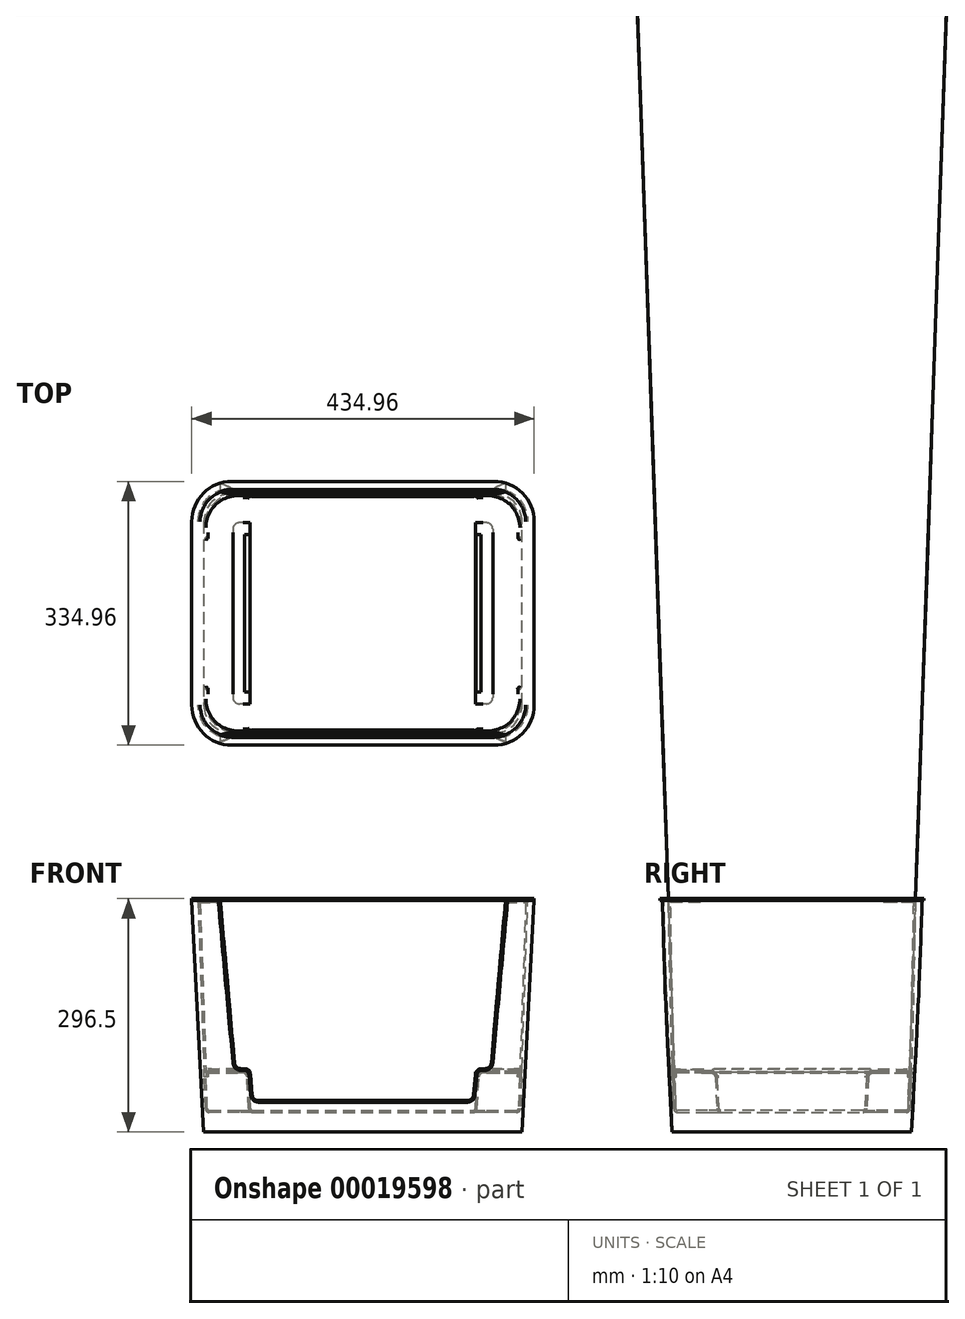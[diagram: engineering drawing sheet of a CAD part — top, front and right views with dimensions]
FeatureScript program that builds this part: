
annotation { "Feature Type Name" : "Feature", "Feature Type Description" : "" }
export const myFeature = defineFeature(function(context is Context, id is Id, definition is map)
    precondition{}
    {
        {
            var Q0;
            Q0=qCreatedBy(makeId("Front.planeOp"),FACE);
            var sketch = newSketch(context, id + "F0", { "sketchPlane" : qUnion([Q0])});
            skLineSegment(sketch, "E0.rect.bottom", {"start": v(150, -100) * mm, "end": v(-150, -100) * mm});
            skLineSegment(sketch, "E0.rect.top", {"start": v(150, 100) * mm, "end": v(-150, 100) * mm});
            skLineSegment(sketch, "E0.rect.left", {"start": v(150, -100) * mm, "end": v(150, 100) * mm});
            skLineSegment(sketch, "E0.rect.right", {"start": v(-150, -100) * mm, "end": v(-150, 100) * mm});
            skPoint(sketch, "E0.rect.middle", {"position": v(0, 0) * mm});
            skSolve(sketch);
        }
        {
            var Q0;
            Q0 = qSketchRegion(id + "F0", true);
            extrude(context, id + "F1", {"entities" : qUnion([Q0]), "endBound" : BoundingType.SYMMETRIC, "depth" : 200 * mm});
        }
        {
            var Q0;
            Q0=makeQuery(id+"F1.opExtrude","SWEPT_FACE",FACE,{"disambiguationData":[OSD([sQuery(id+"F0.wireOp",EDGE,"E0.rect.bottom")])]});
            var sketch = newSketch(context, id + "F2", { "sketchPlane" : qUnion([Q0])});
            skLineSegment(sketch, "E1.rect.bottom", {"start": v(165, -115) * mm, "end": v(-165, -115) * mm});
            skLineSegment(sketch, "E1.rect.top", {"start": v(165, 115) * mm, "end": v(-165, 115) * mm});
            skLineSegment(sketch, "E1.rect.left", {"start": v(165, -115) * mm, "end": v(165, 115) * mm});
            skLineSegment(sketch, "E1.rect.right", {"start": v(-165, -115) * mm, "end": v(-165, 115) * mm});
            skPoint(sketch, "E1.rect.middle", {"position": v(0, 0) * mm});
            skSolve(sketch);
        }
        {
            var Q0;
            Q0 = qSketchRegion(id + "F2", true);
            extrude(context, id + "F3", {"entities" : qUnion([Q0]), "depth" : 1.5 * mm});
        }
        {
            var Q0;
            Q0=makeQuery(id+"F3.opExtrude","SWEPT_EDGE",EDGE,{"disambiguationData":[OSD([sQuery(id+"F2.wireOp",EDGE,"E1.rect.top"),sQuery(id+"F2.wireOp",EDGE,"E1.rect.right")])]});
            var Q1;
            Q1=makeQuery(id+"F3.opExtrude","SWEPT_EDGE",EDGE,{"disambiguationData":[OSD([sQuery(id+"F2.wireOp",EDGE,"E1.rect.bottom"),sQuery(id+"F2.wireOp",EDGE,"E1.rect.right")])]});
            var Q2;
            Q2=makeQuery(id+"F3.opExtrude","SWEPT_EDGE",EDGE,{"disambiguationData":[OSD([sQuery(id+"F2.wireOp",EDGE,"E1.rect.top"),sQuery(id+"F2.wireOp",EDGE,"E1.rect.left")])]});
            var Q3;
            Q3=makeQuery(id+"F3.opExtrude","SWEPT_EDGE",EDGE,{"disambiguationData":[OSD([sQuery(id+"F2.wireOp",EDGE,"E1.rect.bottom"),sQuery(id+"F2.wireOp",EDGE,"E1.rect.left")])]});
            fillet(context, id + "F4", {"entities" : qUnion([Q0, Q1, Q2, Q3]), "radius" : 8 * mm, "tangentPropagation" : true, "allowEdgeOverflow" : false});
        }
        {
            var Q0;
            Q0=makeQuery(id+"F3.opExtrude","CAP_FACE",FACE,{"disambiguationData":[OSD([sQuery(id+"F2.wireOp",EDGE,"E1.rect.bottom"),sQuery(id+"F2.wireOp",EDGE,"E1.rect.top"),sQuery(id+"F2.wireOp",EDGE,"E1.rect.left"),sQuery(id+"F2.wireOp",EDGE,"E1.rect.right")])],"isStart":false});
            cPlane(context, id + "F5", {"entities" : qUnion([Q0]), "cplaneType" : CPlaneType.OFFSET, "offset" : 50 * mm, "width" : 150 * mm, "height" : 150 * mm});
        }
        {
            var Q0;
            Q0=qCreatedBy(id+"F5.planeOp",FACE);
            var sketch = newSketch(context, id + "F6", { "sketchPlane" : qUnion([Q0])});
            skLineSegment(sketch, "E2.rect.bottom", {"start": v(200, 150) * mm, "end": v(-200, 150) * mm});
            skLineSegment(sketch, "E2.rect.top", {"start": v(200, -150) * mm, "end": v(-200, -150) * mm});
            skLineSegment(sketch, "E2.rect.left", {"start": v(200, 150) * mm, "end": v(200, -150) * mm});
            skLineSegment(sketch, "E2.rect.right", {"start": v(-200, 150) * mm, "end": v(-200, -150) * mm});
            skPoint(sketch, "E2.rect.middle", {"position": v(0, 0) * mm});
            skSolve(sketch);
        }
        {
            var Q0;
            Q0 = qSketchRegion(id + "F6", true);
            var Q1;
            Q1=makeQuery(id+"F1.opExtrude","SWEPT_FACE",FACE,{"disambiguationData":[OSD([sQuery(id+"F0.wireOp",EDGE,"E0.rect.top")])]});
            extrude(context, id + "F7", {"entities" : qUnion([Q0]), "oppositeDirection" : true, "endBoundEntityFace" : qUnion([Q1]), "depth" : (251.5 + 20) * mm, "hasDraft" : true, "draftAngle" : 2 * degree});
        }
        {
            var Q0;
            Q0=makeQuery(id+"F3.opExtrude","CAP_FACE",FACE,{"disambiguationData":[OSD([sQuery(id+"F2.wireOp",EDGE,"E1.rect.bottom"),sQuery(id+"F2.wireOp",EDGE,"E1.rect.top"),sQuery(id+"F2.wireOp",EDGE,"E1.rect.left"),sQuery(id+"F2.wireOp",EDGE,"E1.rect.right")])],"isStart":true});
            var sketch = newSketch(context, id + "F8", { "sketchPlane" : qUnion([Q0])});
            skLineSegment(sketch, "E3.rect.bottom", {"start": v(157, 107) * mm, "end": v(-157, 107) * mm, "construction": true});
            skLineSegment(sketch, "E3.rect.top", {"start": v(157, -107) * mm, "end": v(-157, -107) * mm, "construction": true});
            skLineSegment(sketch, "E3.rect.left", {"start": v(157, 107) * mm, "end": v(157, -107) * mm, "construction": true});
            skLineSegment(sketch, "E3.rect.right", {"start": v(-157, 107) * mm, "end": v(-157, -107) * mm, "construction": true});
            skPoint(sketch, "E3.rect.middle", {"position": v(0, 0) * mm});
            skCircle(sketch, "E4", {"center": v(-157, 107) * mm, "radius": 5 * mm});
            skCircle(sketch, "E5", {"center": v(-157, -107) * mm, "radius": 5 * mm});
            skCircle(sketch, "E6", {"center": v(157, -107) * mm, "radius": 5 * mm});
            skCircle(sketch, "E7", {"center": v(157, 107) * mm, "radius": 5 * mm});
            skSolve(sketch);
        }
        {
            var Q0;
            Q0=makeQuery(id+"F7.opExtrude","CAP_FACE",FACE,{"disambiguationData":[OSD([sQuery(id+"F6.wireOp",EDGE,"E2.rect.bottom"),sQuery(id+"F6.wireOp",EDGE,"E2.rect.top"),sQuery(id+"F6.wireOp",EDGE,"E2.rect.left"),sQuery(id+"F6.wireOp",EDGE,"E2.rect.right")])],"isStart":true});
            var sketch = newSketch(context, id + "F9", { "sketchPlane" : qUnion([Q0])});
            skLineSegment(sketch, "E8", {"start": v(0, 0) * mm, "end": v(0, -159.48) * mm, "construction": true});
            skLineSegment(sketch, "E9", {"start": v(0, 0) * mm, "end": v(209.48, 0) * mm, "construction": true});
            skLineSegment(sketch, "E10", {"start": v(-209.48, -159.48) * mm, "end": v(-209.48, -95) * mm});
            skLineSegment(sketch, "E11", {"start": v(-209.48, -95) * mm, "end": v(-157, -95) * mm});
            skLineSegment(sketch, "E12", {"start": v(-145, -107) * mm, "end": v(-145, -159.48) * mm});
            skLineSegment(sketch, "E13", {"start": v(-145, -159.48) * mm, "end": v(-209.48, -159.48) * mm});
            skPoint(sketch, "E14.visualSharp", {"position": v(-145, -95) * mm});
            skArc(sketch, "E14.filletArc", {"start": v(-145, -107) * mm, "mid": v(-148.51, -98.51) * mm, "end": v(-157, -95) * mm});
            skLineSegment(sketch, "E15.MirrorCS", {"start": v(145, -107) * mm, "end": v(145, -159.48) * mm});
            skArc(sketch, "E16.MirrorCS", {"start": v(145, -107) * mm, "mid": v(148.51, -98.51) * mm, "end": v(157, -95) * mm});
            skPoint(sketch, "E17.MirrorP", {"position": v(145, -95) * mm});
            skLineSegment(sketch, "E18.MirrorCS", {"start": v(145, -159.48) * mm, "end": v(209.48, -159.48) * mm});
            skLineSegment(sketch, "E19.MirrorCS", {"start": v(209.48, -159.48) * mm, "end": v(209.48, -95) * mm});
            skLineSegment(sketch, "E20.MirrorCS", {"start": v(209.48, -95) * mm, "end": v(157, -95) * mm});
            skPoint(sketch, "E21.MirrorP", {"position": v(145, 95) * mm});
            skPoint(sketch, "E22.MirrorP", {"position": v(-145, 95) * mm});
            skLineSegment(sketch, "E23.MirrorCS", {"start": v(209.48, 159.48) * mm, "end": v(209.48, 95) * mm});
            skArc(sketch, "E24.MirrorCS", {"start": v(145, 107) * mm, "mid": v(148.51, 98.51) * mm, "end": v(157, 95) * mm});
            skLineSegment(sketch, "E25.MirrorCS", {"start": v(-145, 159.48) * mm, "end": v(-209.48, 159.48) * mm});
            skLineSegment(sketch, "E26.MirrorCS", {"start": v(-145, 107) * mm, "end": v(-145, 159.48) * mm});
            skLineSegment(sketch, "E27.MirrorCS", {"start": v(-209.48, 159.48) * mm, "end": v(-209.48, 95) * mm});
            skLineSegment(sketch, "E28.MirrorCS", {"start": v(209.48, 95) * mm, "end": v(157, 95) * mm});
            skLineSegment(sketch, "E29.MirrorCS", {"start": v(-209.48, 95) * mm, "end": v(-157, 95) * mm});
            skArc(sketch, "E30.MirrorCS", {"start": v(-145, 107) * mm, "mid": v(-148.51, 98.51) * mm, "end": v(-157, 95) * mm});
            skLineSegment(sketch, "E31.MirrorCS", {"start": v(145, 159.48) * mm, "end": v(209.48, 159.48) * mm});
            skLineSegment(sketch, "E32.MirrorCS", {"start": v(145, 107) * mm, "end": v(145, 159.48) * mm});
            skSolve(sketch);
        }
        {
            var Q0;
            Q0 = qSketchRegion(id + "F9", true);
            var Q1;
            Q1=makeQuery(id+"F3.opExtrude","CAP_FACE",FACE,{"disambiguationData":[OSD([sQuery(id+"F2.wireOp",EDGE,"E1.rect.bottom"),sQuery(id+"F2.wireOp",EDGE,"E1.rect.top"),sQuery(id+"F2.wireOp",EDGE,"E1.rect.left"),sQuery(id+"F2.wireOp",EDGE,"E1.rect.right")])],"isStart":false});
            extrude(context, id + "F10", {"entities" : qUnion([Q0]), "operationType" : NewBodyOperationType.REMOVE, "endBound" : BoundingType.UP_TO_SURFACE, "oppositeDirection" : true, "endBoundEntityFace" : qUnion([Q1]), "depth" : 25 * mm, "hasDraft" : true, "draftAngle" : 3 * degree, "draftPullDirection" : true});
        }
        {
            var Q0;
            Q0=makeQuery(id+"F7.opExtrude","CAP_FACE",FACE,{"disambiguationData":[OSD([sQuery(id+"F6.wireOp",EDGE,"E2.rect.bottom"),sQuery(id+"F6.wireOp",EDGE,"E2.rect.top"),sQuery(id+"F6.wireOp",EDGE,"E2.rect.left"),sQuery(id+"F6.wireOp",EDGE,"E2.rect.right")])],"isStart":false});
            var sketch = newSketch(context, id + "F11", { "sketchPlane" : qUnion([Q0])});
            skLineSegment(sketch, "E33.0", {"start": v(217.48, -167.48) * mm, "end": v(217.48, 167.48) * mm});
            skLineSegment(sketch, "E33.1", {"start": v(-217.48, -167.48) * mm, "end": v(217.48, -167.48) * mm});
            skLineSegment(sketch, "E33.2", {"start": v(-217.48, 167.48) * mm, "end": v(-217.48, -167.48) * mm});
            skLineSegment(sketch, "E33.3", {"start": v(217.48, 167.48) * mm, "end": v(-217.48, 167.48) * mm});
            skSolve(sketch);
        }
        {
            var Q0;
            Q0 = qSketchRegion(id + "F11", true);
            extrude(context, id + "F12", {"entities" : qUnion([Q0]), "operationType" : NewBodyOperationType.ADD, "oppositeDirection" : true, "depth" : 2.5 * mm});
        }
        {
            var Q0;
            Q0=makeQuery(id+"F7.opExtrude","SWEPT_EDGE",EDGE,{"disambiguationData":[OSD([sQuery(id+"F6.wireOp",EDGE,"E2.rect.bottom"),sQuery(id+"F6.wireOp",EDGE,"E2.rect.right")])]});
            var Q1;
            Q1=makeQuery(id+"F7.opExtrude","SWEPT_EDGE",EDGE,{"disambiguationData":[OSD([sQuery(id+"F6.wireOp",EDGE,"E2.rect.bottom"),sQuery(id+"F6.wireOp",EDGE,"E2.rect.left")])]});
            var Q2;
            Q2=makeQuery(id+"F7.opExtrude","SWEPT_EDGE",EDGE,{"disambiguationData":[OSD([sQuery(id+"F6.wireOp",EDGE,"E2.rect.top"),sQuery(id+"F6.wireOp",EDGE,"E2.rect.left")])]});
            var Q3;
            Q3=makeQuery(id+"F7.opExtrude","SWEPT_EDGE",EDGE,{"disambiguationData":[OSD([sQuery(id+"F6.wireOp",EDGE,"E2.rect.top"),sQuery(id+"F6.wireOp",EDGE,"E2.rect.right")])]});
            fillet(context, id + "F13", {"entities" : qUnion([Q0, Q1, Q2, Q3]), "radius" : 43 * mm, "tangentPropagation" : true, "allowEdgeOverflow" : false});
        }
        {
            var Q0;
            Q0=makeQuery(id+"F7.opExtrude","CAP_EDGE",EDGE,{"disambiguationData":[OSD([sQuery(id+"F6.wireOp",EDGE,"E2.rect.right")])],"isStart":true});
            var Q1;
            Q1=makeQuery(id+"F7.opExtrude","CAP_EDGE",EDGE,{"disambiguationData":[OSD([sQuery(id+"F6.wireOp",EDGE,"E2.rect.bottom")])],"isStart":true});
            var Q2;
            Q2=makeQuery(id+"F7.opExtrude","CAP_EDGE",EDGE,{"disambiguationData":[OSD([sQuery(id+"F6.wireOp",EDGE,"E2.rect.top")])],"isStart":true});
            var Q3;
            Q3=makeQuery(id+"F7.opExtrude","CAP_EDGE",EDGE,{"disambiguationData":[OSD([sQuery(id+"F6.wireOp",EDGE,"E2.rect.left")])],"isStart":true});
            fillet(context, id + "F14", {"entities" : qUnion([Q0, Q1, Q2, Q3]), "radius" : 5 * mm, "tangentPropagation" : true, "allowEdgeOverflow" : false});
        }
        {
            var Q0;
            Q0=makeQuery(id+"F10.boolean.opBoolean","COPY",EDGE,{"derivedFrom":makeQuery(id+"F10.opExtrude","CAP_EDGE",EDGE,{"disambiguationData":[OSD([sQuery(id+"F9.wireOp",EDGE,"E29.MirrorCS")])],"isStart":false})});
            var Q1;
            Q1=makeQuery(id+"F10.boolean.opBoolean","COPY",EDGE,{"derivedFrom":makeQuery(id+"F10.opExtrude","CAP_EDGE",EDGE,{"disambiguationData":[OSD([sQuery(id+"F9.wireOp",EDGE,"E12")])],"isStart":false})});
            var Q2;
            Q2=makeQuery(id+"F10.boolean.opBoolean","COPY",EDGE,{"derivedFrom":makeQuery(id+"F10.opExtrude","CAP_EDGE",EDGE,{"disambiguationData":[OSD([sQuery(id+"F9.wireOp",EDGE,"E32.MirrorCS")])],"isStart":false})});
            var Q3;
            Q3=makeQuery(id+"F10.boolean.opBoolean","COPY",EDGE,{"derivedFrom":makeQuery(id+"F10.opExtrude","CAP_EDGE",EDGE,{"disambiguationData":[OSD([sQuery(id+"F9.wireOp",EDGE,"E15.MirrorCS")])],"isStart":false})});
            fillet(context, id + "F15", {"entities" : qUnion([Q0, Q1, Q2, Q3]), "radius" : 5 * mm, "tangentPropagation" : true, "allowEdgeOverflow" : false});
        }
        {
            var Q0;
            Q0=makeQuery(id+"F13.opFillet","BLEND_EDGE",EDGE,{"blendedFrom":[makeQuery(id+"F7.opExtrude","SWEPT_EDGE",EDGE,{"disambiguationData":[OSD([sQuery(id+"F6.wireOp",EDGE,"E2.rect.bottom"),sQuery(id+"F6.wireOp",EDGE,"E2.rect.right")])]}),makeQuery(id+"F10.boolean.opBoolean","COPY",FACE,{"derivedFrom":makeQuery(id+"F10.opExtrude","CAP_FACE",FACE,{"disambiguationData":[OSD([sQuery(id+"F9.wireOp",EDGE,"E25.MirrorCS"),sQuery(id+"F9.wireOp",EDGE,"E26.MirrorCS"),sQuery(id+"F9.wireOp",EDGE,"E27.MirrorCS"),sQuery(id+"F9.wireOp",EDGE,"E29.MirrorCS"),sQuery(id+"F9.wireOp",EDGE,"E30.MirrorCS")])],"isStart":false})})],"blendedInto":[makeQuery(id+"F10.boolean.opBoolean","COPY",FACE,{"derivedFrom":makeQuery(id+"F10.opExtrude","CAP_FACE",FACE,{"disambiguationData":[OSD([sQuery(id+"F9.wireOp",EDGE,"E25.MirrorCS"),sQuery(id+"F9.wireOp",EDGE,"E26.MirrorCS"),sQuery(id+"F9.wireOp",EDGE,"E27.MirrorCS"),sQuery(id+"F9.wireOp",EDGE,"E29.MirrorCS"),sQuery(id+"F9.wireOp",EDGE,"E30.MirrorCS")])],"isStart":false})})]});
            var Q1;
            Q1=makeQuery(id+"F13.opFillet","BLEND_EDGE",EDGE,{"blendedFrom":[makeQuery(id+"F7.opExtrude","SWEPT_EDGE",EDGE,{"disambiguationData":[OSD([sQuery(id+"F6.wireOp",EDGE,"E2.rect.bottom"),sQuery(id+"F6.wireOp",EDGE,"E2.rect.left")])]}),makeQuery(id+"F10.boolean.opBoolean","COPY",FACE,{"derivedFrom":makeQuery(id+"F10.opExtrude","CAP_FACE",FACE,{"disambiguationData":[OSD([sQuery(id+"F9.wireOp",EDGE,"E23.MirrorCS"),sQuery(id+"F9.wireOp",EDGE,"E24.MirrorCS"),sQuery(id+"F9.wireOp",EDGE,"E28.MirrorCS"),sQuery(id+"F9.wireOp",EDGE,"E31.MirrorCS"),sQuery(id+"F9.wireOp",EDGE,"E32.MirrorCS")])],"isStart":false})})],"blendedInto":[makeQuery(id+"F10.boolean.opBoolean","COPY",FACE,{"derivedFrom":makeQuery(id+"F10.opExtrude","CAP_FACE",FACE,{"disambiguationData":[OSD([sQuery(id+"F9.wireOp",EDGE,"E23.MirrorCS"),sQuery(id+"F9.wireOp",EDGE,"E24.MirrorCS"),sQuery(id+"F9.wireOp",EDGE,"E28.MirrorCS"),sQuery(id+"F9.wireOp",EDGE,"E31.MirrorCS"),sQuery(id+"F9.wireOp",EDGE,"E32.MirrorCS")])],"isStart":false})})]});
            var Q2;
            Q2=makeQuery(id+"F13.opFillet","BLEND_EDGE",EDGE,{"blendedFrom":[makeQuery(id+"F7.opExtrude","SWEPT_EDGE",EDGE,{"disambiguationData":[OSD([sQuery(id+"F6.wireOp",EDGE,"E2.rect.top"),sQuery(id+"F6.wireOp",EDGE,"E2.rect.left")])]}),makeQuery(id+"F10.boolean.opBoolean","COPY",FACE,{"derivedFrom":makeQuery(id+"F10.opExtrude","CAP_FACE",FACE,{"disambiguationData":[OSD([sQuery(id+"F9.wireOp",EDGE,"E15.MirrorCS"),sQuery(id+"F9.wireOp",EDGE,"E16.MirrorCS"),sQuery(id+"F9.wireOp",EDGE,"E18.MirrorCS"),sQuery(id+"F9.wireOp",EDGE,"E19.MirrorCS"),sQuery(id+"F9.wireOp",EDGE,"E20.MirrorCS")])],"isStart":false})})],"blendedInto":[makeQuery(id+"F10.boolean.opBoolean","COPY",FACE,{"derivedFrom":makeQuery(id+"F10.opExtrude","CAP_FACE",FACE,{"disambiguationData":[OSD([sQuery(id+"F9.wireOp",EDGE,"E15.MirrorCS"),sQuery(id+"F9.wireOp",EDGE,"E16.MirrorCS"),sQuery(id+"F9.wireOp",EDGE,"E18.MirrorCS"),sQuery(id+"F9.wireOp",EDGE,"E19.MirrorCS"),sQuery(id+"F9.wireOp",EDGE,"E20.MirrorCS")])],"isStart":false})})]});
            var Q3;
            Q3=makeQuery(id+"F13.opFillet","BLEND_EDGE",EDGE,{"blendedFrom":[makeQuery(id+"F7.opExtrude","SWEPT_EDGE",EDGE,{"disambiguationData":[OSD([sQuery(id+"F6.wireOp",EDGE,"E2.rect.top"),sQuery(id+"F6.wireOp",EDGE,"E2.rect.right")])]}),makeQuery(id+"F10.boolean.opBoolean","COPY",FACE,{"derivedFrom":makeQuery(id+"F10.opExtrude","CAP_FACE",FACE,{"disambiguationData":[OSD([sQuery(id+"F9.wireOp",EDGE,"E10"),sQuery(id+"F9.wireOp",EDGE,"E11"),sQuery(id+"F9.wireOp",EDGE,"E12"),sQuery(id+"F9.wireOp",EDGE,"E13"),sQuery(id+"F9.wireOp",EDGE,"E14.filletArc")])],"isStart":false})})],"blendedInto":[makeQuery(id+"F10.boolean.opBoolean","COPY",FACE,{"derivedFrom":makeQuery(id+"F10.opExtrude","CAP_FACE",FACE,{"disambiguationData":[OSD([sQuery(id+"F9.wireOp",EDGE,"E10"),sQuery(id+"F9.wireOp",EDGE,"E11"),sQuery(id+"F9.wireOp",EDGE,"E12"),sQuery(id+"F9.wireOp",EDGE,"E13"),sQuery(id+"F9.wireOp",EDGE,"E14.filletArc")])],"isStart":false})})]});
            fillet(context, id + "F16", {"entities" : qUnion([Q0, Q1, Q2, Q3]), "radius" : 5 * mm, "tangentPropagation" : true, "allowEdgeOverflow" : false});
        }
        {
            var Q0;
            Q0=makeQuery(id+"F12.opExtrude","SWEPT_EDGE",EDGE,{"disambiguationData":[OSD([sQuery(id+"F11.wireOp",EDGE,"E33.1"),sQuery(id+"F11.wireOp",EDGE,"E33.2")])]});
            var Q1;
            Q1=makeQuery(id+"F12.opExtrude","SWEPT_EDGE",EDGE,{"disambiguationData":[OSD([sQuery(id+"F11.wireOp",EDGE,"E33.0"),sQuery(id+"F11.wireOp",EDGE,"E33.1")])]});
            var Q2;
            Q2=makeQuery(id+"F12.opExtrude","SWEPT_EDGE",EDGE,{"disambiguationData":[OSD([sQuery(id+"F11.wireOp",EDGE,"E33.0"),sQuery(id+"F11.wireOp",EDGE,"E33.3")])]});
            var Q3;
            Q3=makeQuery(id+"F12.opExtrude","SWEPT_EDGE",EDGE,{"disambiguationData":[OSD([sQuery(id+"F11.wireOp",EDGE,"E33.2"),sQuery(id+"F11.wireOp",EDGE,"E33.3")])]});
            fillet(context, id + "F17", {"entities" : qUnion([Q0, Q1, Q2, Q3]), "radius" : (43 + 8) * mm, "tangentPropagation" : true, "allowEdgeOverflow" : false});
        }
        {
            var Q0;
            Q0=makeQuery(id+"F13.opFillet","BLEND_EDGE",EDGE,{"blendedFrom":[makeQuery(id+"F7.opExtrude","SWEPT_EDGE",EDGE,{"disambiguationData":[OSD([sQuery(id+"F6.wireOp",EDGE,"E2.rect.bottom"),sQuery(id+"F6.wireOp",EDGE,"E2.rect.right")])]}),makeQuery(id+"F12.opExtrude","CAP_FACE",FACE,{"disambiguationData":[OSD([sQuery(id+"F11.wireOp",EDGE,"E33.0"),sQuery(id+"F11.wireOp",EDGE,"E33.1"),sQuery(id+"F11.wireOp",EDGE,"E33.2"),sQuery(id+"F11.wireOp",EDGE,"E33.3")])],"isStart":false})],"blendedInto":[makeQuery(id+"F12.opExtrude","CAP_FACE",FACE,{"disambiguationData":[OSD([sQuery(id+"F11.wireOp",EDGE,"E33.0"),sQuery(id+"F11.wireOp",EDGE,"E33.1"),sQuery(id+"F11.wireOp",EDGE,"E33.2"),sQuery(id+"F11.wireOp",EDGE,"E33.3")])],"isStart":false})]});
            fillet(context, id + "F18", {"entities" : qUnion([Q0]), "radius" : 2.5 * mm, "tangentPropagation" : true, "allowEdgeOverflow" : false});
        }
        {
            var Q0;
            Q0=makeQuery(id+"F7.opExtrude","SWEPT_BODY",BODY,{"disambiguationData":[OSD([sQuery(id+"F6.wireOp",EDGE,"E2.rect.bottom"),sQuery(id+"F6.wireOp",EDGE,"E2.rect.top"),sQuery(id+"F6.wireOp",EDGE,"E2.rect.left"),sQuery(id+"F6.wireOp",EDGE,"E2.rect.right")])]});
            transform(context, id + "F19", {"entities" : qUnion([Q0]), "transformType" : TransformType.COPY});
        }
        {
            var Q0;
            Q0=makeQuery(id+"F7.opExtrude","CAP_FACE",FACE,{"disambiguationData":[OSD([sQuery(id+"F6.wireOp",EDGE,"E2.rect.bottom"),sQuery(id+"F6.wireOp",EDGE,"E2.rect.top"),sQuery(id+"F6.wireOp",EDGE,"E2.rect.left"),sQuery(id+"F6.wireOp",EDGE,"E2.rect.right")])],"isStart":false});
            shell(context, id + "F20", {"entities" : qUnion([Q0]), "thickness" : 2.5 * mm});
        }
        {
            var Q0;
            Q0=makeQuery(id+"F12.opExtrude","CAP_FACE",FACE,{"disambiguationData":[OSD([sQuery(id+"F11.wireOp",EDGE,"E33.0"),sQuery(id+"F11.wireOp",EDGE,"E33.1"),sQuery(id+"F11.wireOp",EDGE,"E33.2"),sQuery(id+"F11.wireOp",EDGE,"E33.3")])],"isStart":false});
            var sketch = newSketch(context, id + "F21", { "sketchPlane" : qUnion([Q0])});
            skArc(sketch, "E34.0", {"start": v(-166.48, 167.48) * mm, "mid": v(-202.54, 152.54) * mm, "end": v(-217.48, 116.48) * mm});
            skLineSegment(sketch, "E35.0", {"start": v(-166.48, 167.48) * mm, "end": v(166.48, 167.48) * mm});
            skLineSegment(sketch, "E36.0.0", {"start": v(217.48, -116.48) * mm, "end": v(217.48, 116.48) * mm});
            skArc(sketch, "E36.0.1", {"start": v(217.48, 116.48) * mm, "mid": v(202.54, 152.54) * mm, "end": v(166.48, 167.48) * mm});
            skLineSegment(sketch, "E36.0.2", {"start": v(166.48, 167.48) * mm, "end": v(-166.48, 167.48) * mm});
            skLineSegment(sketch, "E36.0.4", {"start": v(-217.48, 116.48) * mm, "end": v(-217.48, -116.48) * mm});
            skArc(sketch, "E36.0.5", {"start": v(-217.48, -116.48) * mm, "mid": v(-202.54, -152.54) * mm, "end": v(-166.48, -167.48) * mm});
            skLineSegment(sketch, "E36.0.6", {"start": v(-166.48, -167.48) * mm, "end": v(166.48, -167.48) * mm});
            skArc(sketch, "E36.0.7", {"start": v(166.48, -167.48) * mm, "mid": v(202.54, -152.54) * mm, "end": v(217.48, -116.48) * mm});
            skSolve(sketch);
        }
        {
            var Q0;
            Q0=makeQuery(id+"F7.opExtrude","CAP_FACE",FACE,{"disambiguationData":[OSD([sQuery(id+"F6.wireOp",EDGE,"E2.rect.bottom"),sQuery(id+"F6.wireOp",EDGE,"E2.rect.top"),sQuery(id+"F6.wireOp",EDGE,"E2.rect.left"),sQuery(id+"F6.wireOp",EDGE,"E2.rect.right")])],"isStart":true});
            cPlane(context, id + "F22", {"entities" : qUnion([Q0]), "cplaneType" : CPlaneType.OFFSET, "offset" : 25 * mm, "width" : 150 * mm, "height" : 150 * mm});
        }
        {
            var Q0;
            Q0 = qSketchRegion(id + "F21", true);
            var Q1;
            Q1=qCreatedBy(id+"F22.planeOp",FACE);
            extrude(context, id + "F23", {"entities" : qUnion([Q0]), "endBound" : BoundingType.UP_TO_SURFACE, "endBoundEntityFace" : qUnion([Q1]), "depth" : 25 * mm, "hasDraft" : true, "draftAngle" : 3 * degree, "draftPullDirection" : true});
        }
        {
            var Q0;
            Q0=makeQuery(id+"F19.opPattern","COPY",BODY,{"derivedFrom":makeQuery(id+"F7.opExtrude","SWEPT_BODY",BODY,{"disambiguationData":[OSD([sQuery(id+"F6.wireOp",EDGE,"E2.rect.bottom"),sQuery(id+"F6.wireOp",EDGE,"E2.rect.top"),sQuery(id+"F6.wireOp",EDGE,"E2.rect.left"),sQuery(id+"F6.wireOp",EDGE,"E2.rect.right")])]}),"instanceName":"1"});
            var Q1;
            Q1=makeQuery(id+"F23.opExtrude","SWEPT_BODY",BODY,{"disambiguationData":[OSD([sQuery(id+"F21.wireOp",EDGE,"E36.0.0"),sQuery(id+"F21.wireOp",EDGE,"E36.0.1"),sQuery(id+"F21.wireOp",EDGE,"E36.0.2"),sQuery(id+"F21.wireOp",EDGE,"E34.0"),sQuery(id+"F21.wireOp",EDGE,"E36.0.4"),sQuery(id+"F21.wireOp",EDGE,"E36.0.5"),sQuery(id+"F21.wireOp",EDGE,"E36.0.6"),sQuery(id+"F21.wireOp",EDGE,"E36.0.7")])]});
            booleanBodies(context, id + "F24", {"operationType" : BooleanOperationType.SUBTRACTION, "tools" : qUnion([Q0]), "targets" : qUnion([Q1])});
        }
        {
            var Q0;
            Q0=qCreatedBy(makeId("Front.planeOp"),FACE);
            var sketch = newSketch(context, id + "F25", { "sketchPlane" : qUnion([Q0])});
            skLineSegment(sketch, "E37", {"start": v(-181.18, 117.5) * mm, "end": v(-162.5, -96) * mm});
            skLineSegment(sketch, "E38", {"start": v(-140, -136.5) * mm, "end": v(140, -136.5) * mm});
            skLineSegment(sketch, "E39", {"start": v(0, 0) * mm, "end": v(0, 179.59) * mm, "construction": true});
            skLineSegment(sketch, "E40.MirrorCS", {"start": v(181.18, 117.5) * mm, "end": v(162.5, -96) * mm});
            skLineSegment(sketch, "E41", {"start": v(-181.18, 117.5) * mm, "end": v(181.18, 117.5) * mm});
            skLineSegment(sketch, "E42", {"start": v(-162.5, -96) * mm, "end": v(-143.54, -96) * mm});
            skLineSegment(sketch, "E43", {"start": v(-143.54, -96) * mm, "end": v(-140, -136.5) * mm});
            skPoint(sketch, "E44.orphan", {"position": v(-158.96, -136.5) * mm});
            skLineSegment(sketch, "E45.MirrorCS", {"start": v(162.5, -96) * mm, "end": v(143.54, -96) * mm});
            skLineSegment(sketch, "E46.MirrorCS", {"start": v(143.54, -96) * mm, "end": v(140, -136.5) * mm});
            skPoint(sketch, "E47.orphan", {"position": v(158.96, -136.5) * mm});
            skSolve(sketch);
        }
        {
            var Q0;
            Q0 = qSketchRegion(id + "F25", true);
            extrude(context, id + "F26", {"entities" : qUnion([Q0]), "operationType" : NewBodyOperationType.REMOVE, "endBound" : BoundingType.SYMMETRIC, "oppositeDirection" : true, "depth" : 500 * mm});
        }
        {
            var Q0;
            Q0=makeQuery(id+"F26.boolean.opBoolean","COPY",EDGE,{"disambiguationData":[OD(0.0)],"derivedFrom":makeQuery(id+"F26.opExtrude","SWEPT_EDGE",EDGE,{"disambiguationData":[OSD([sQuery(id+"F25.wireOp",EDGE,"E42"),sQuery(id+"F25.wireOp",EDGE,"E43")])]})});
            var Q1;
            Q1=makeQuery(id+"F26.boolean.opBoolean","COPY",EDGE,{"disambiguationData":[OD(0.0)],"derivedFrom":makeQuery(id+"F26.opExtrude","SWEPT_EDGE",EDGE,{"disambiguationData":[OSD([sQuery(id+"F25.wireOp",EDGE,"E45.MirrorCS"),sQuery(id+"F25.wireOp",EDGE,"E46.MirrorCS")])]})});
            var Q2;
            Q2=makeQuery(id+"F26.boolean.opBoolean","COPY",EDGE,{"disambiguationData":[OD(1.0)],"derivedFrom":makeQuery(id+"F26.opExtrude","SWEPT_EDGE",EDGE,{"disambiguationData":[OSD([sQuery(id+"F25.wireOp",EDGE,"E45.MirrorCS"),sQuery(id+"F25.wireOp",EDGE,"E46.MirrorCS")])]})});
            var Q3;
            Q3=makeQuery(id+"F26.boolean.opBoolean","COPY",EDGE,{"disambiguationData":[OD(1.0)],"derivedFrom":makeQuery(id+"F26.opExtrude","SWEPT_EDGE",EDGE,{"disambiguationData":[OSD([sQuery(id+"F25.wireOp",EDGE,"E42"),sQuery(id+"F25.wireOp",EDGE,"E43")])]})});
            var Q4;
            Q4=makeQuery(id+"F26.boolean.opBoolean","COPY",EDGE,{"disambiguationData":[OD(1.0)],"derivedFrom":makeQuery(id+"F26.opExtrude","SWEPT_EDGE",EDGE,{"disambiguationData":[OSD([sQuery(id+"F25.wireOp",EDGE,"E38"),sQuery(id+"F25.wireOp",EDGE,"E43")])]})});
            var Q5;
            Q5=makeQuery(id+"F26.boolean.opBoolean","COPY",EDGE,{"disambiguationData":[OD(1.0)],"derivedFrom":makeQuery(id+"F26.opExtrude","SWEPT_EDGE",EDGE,{"disambiguationData":[OSD([sQuery(id+"F25.wireOp",EDGE,"E38"),sQuery(id+"F25.wireOp",EDGE,"E46.MirrorCS")])]})});
            var Q6;
            Q6=makeQuery(id+"F26.boolean.opBoolean","COPY",EDGE,{"disambiguationData":[OD(0.0)],"derivedFrom":makeQuery(id+"F26.opExtrude","SWEPT_EDGE",EDGE,{"disambiguationData":[OSD([sQuery(id+"F25.wireOp",EDGE,"E40.MirrorCS"),sQuery(id+"F25.wireOp",EDGE,"E45.MirrorCS")])]})});
            var Q7;
            Q7=makeQuery(id+"F26.boolean.opBoolean","COPY",EDGE,{"disambiguationData":[OD(0.0)],"derivedFrom":makeQuery(id+"F26.opExtrude","SWEPT_EDGE",EDGE,{"disambiguationData":[OSD([sQuery(id+"F25.wireOp",EDGE,"E38"),sQuery(id+"F25.wireOp",EDGE,"E46.MirrorCS")])]})});
            var Q8;
            Q8=makeQuery(id+"F26.boolean.opBoolean","COPY",EDGE,{"disambiguationData":[OD(0.0)],"derivedFrom":makeQuery(id+"F26.opExtrude","SWEPT_EDGE",EDGE,{"disambiguationData":[OSD([sQuery(id+"F25.wireOp",EDGE,"E37"),sQuery(id+"F25.wireOp",EDGE,"E42")])]})});
            var Q9;
            Q9=makeQuery(id+"F26.boolean.opBoolean","COPY",EDGE,{"disambiguationData":[OD(0.0)],"derivedFrom":makeQuery(id+"F26.opExtrude","SWEPT_EDGE",EDGE,{"disambiguationData":[OSD([sQuery(id+"F25.wireOp",EDGE,"E38"),sQuery(id+"F25.wireOp",EDGE,"E43")])]})});
            fillet(context, id + "F27", {"entities" : qUnion([Q0, Q1, Q2, Q3, Q4, Q5, Q6, Q7, Q8, Q9]), "radius" : 8 * mm, "tangentPropagation" : true, "allowEdgeOverflow" : false});
        }
        {
            var Q0;
            Q0=makeQuery(id+"F26.boolean.opBoolean","INTERSECT",EDGE,{"derivedFrom":[makeQuery(id+"F23.opExtrude","SWEPT_FACE",FACE,{"disambiguationData":[OSD([sQuery(id+"F21.wireOp",EDGE,"E34.0")])]}),makeQuery(id+"F26.opExtrude","SWEPT_FACE",FACE,{"disambiguationData":[OSD([sQuery(id+"F25.wireOp",EDGE,"E37")])]})]});
            chamfer(context, id + "F28", {"entities" : qUnion([Q0]), "width" : 2 * mm, "tangentPropagation" : true});
        }
    });
